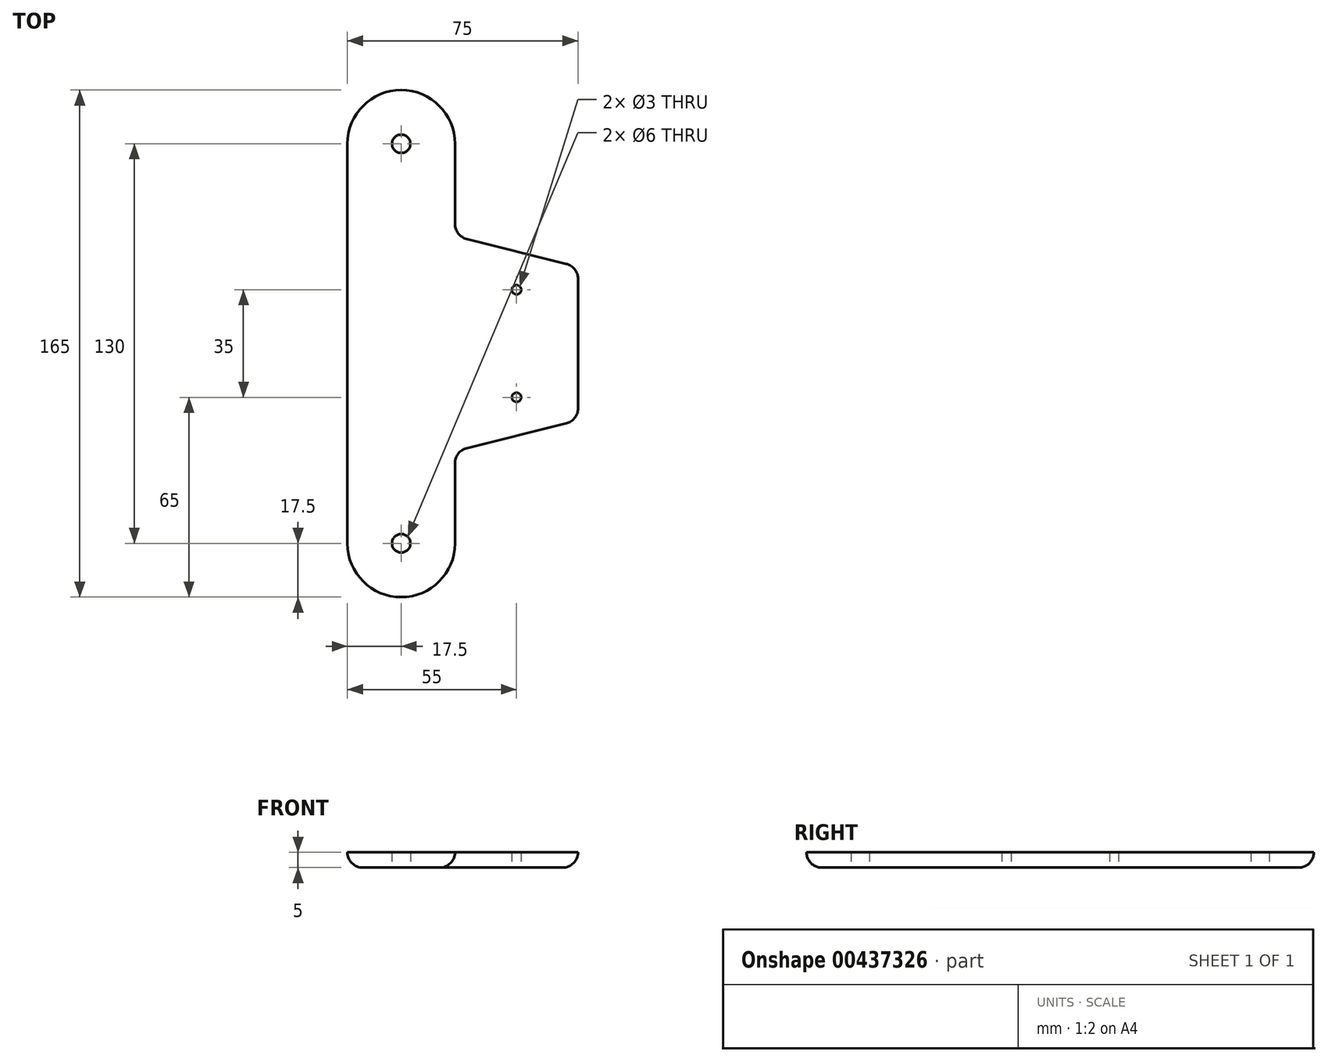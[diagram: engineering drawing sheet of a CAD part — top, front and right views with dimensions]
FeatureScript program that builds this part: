
annotation { "Feature Type Name" : "Feature", "Feature Type Description" : "" }
export const myFeature = defineFeature(function(context is Context, id is Id, definition is map)
    precondition{}
    {
        {
            var Q0;
            Q0=qCreatedBy(makeId("Top.planeOp"),FACE);
            var sketch = newSketch(context, id + "F0", { "sketchPlane" : qUnion([Q0])});
            skLineSegment(sketch, "E0.left", {"start": v(17.5, 65) * mm, "end": v(17.5, -65) * mm});
            skLineSegment(sketch, "E0.right", {"start": v(-17.5, 65) * mm, "end": v(-17.5, 38.9) * mm});
            skPoint(sketch, "E0.middle", {"position": v(0, 0) * mm});
            skArc(sketch, "E1", {"start": v(-17.5, -65) * mm, "mid": v(0, -82.5) * mm, "end": v(17.5, -65) * mm});
            skLineSegment(sketch, "E2.0", {"start": v(-57.5, 21.1) * mm, "end": v(-57.5, -21.1) * mm});
            skArc(sketch, "E3", {"start": v(17.5, 65) * mm, "mid": v(0, 82.5) * mm, "end": v(-17.5, 65) * mm});
            skLineSegment(sketch, "E4", {"start": v(-53.71, -25.95) * mm, "end": v(-21.29, -34.05) * mm});
            skLineSegment(sketch, "E5", {"start": v(-53.71, 25.95) * mm, "end": v(-21.29, 34.05) * mm});
            skLineSegment(sketch, "E6.trimOffspring", {"start": v(-17.5, -38.9) * mm, "end": v(-17.5, -65) * mm});
            skPoint(sketch, "E7.visualSharp", {"position": v(-57.5, 25) * mm});
            skArc(sketch, "E7.filletArc", {"start": v(-53.71, 25.95) * mm, "mid": v(-56.44, 24.17) * mm, "end": v(-57.5, 21.1) * mm});
            skPoint(sketch, "E8.visualSharp", {"position": v(-57.5, -25) * mm});
            skArc(sketch, "E8.filletArc", {"start": v(-57.5, -21.1) * mm, "mid": v(-56.44, -24.17) * mm, "end": v(-53.71, -25.95) * mm});
            skPoint(sketch, "E9.visualSharp", {"position": v(-17.5, -35) * mm});
            skArc(sketch, "E9.filletArc", {"start": v(-17.5, -38.9) * mm, "mid": v(-18.56, -35.83) * mm, "end": v(-21.29, -34.05) * mm});
            skPoint(sketch, "E10.visualSharp", {"position": v(-17.5, 35) * mm});
            skArc(sketch, "E10.filletArc", {"start": v(-21.29, 34.05) * mm, "mid": v(-18.56, 35.83) * mm, "end": v(-17.5, 38.9) * mm});
            skPoint(sketch, "E11", {"position": v(-57.5, 0) * mm});
            skPoint(sketch, "E12", {"position": v(-37.5, 0) * mm});
            skCircle(sketch, "E13", {"center": v(-37.5, 17.5) * mm, "radius": 1.5 * mm});
            skLineSegment(sketch, "E14", {"start": v(-57.5, 0) * mm, "end": v(0, 0) * mm, "construction": true});
            skCircle(sketch, "E15.MirrorC", {"center": v(-37.5, -17.5) * mm, "radius": 1.5 * mm});
            skCircle(sketch, "E16", {"center": v(0, 65) * mm, "radius": 3 * mm});
            skCircle(sketch, "E17", {"center": v(0, -65) * mm, "radius": 3 * mm});
            skSolve(sketch);
        }
        {
            var Q0;
            Q0=makeQuery(id+"F0.imprint","IMPRINT",FACE,{"disambiguationData":[TD([[makeQuery(id+"F0.imprint","IMPRINT",EDGE,{"derivedFrom":sQuery(id+"F0.wireOp",EDGE,"E0.left")}),-1.0]])]});
            extrude(context, id + "F1", {"entities" : qUnion([Q0]), "depth" : 5 * mm});
        }
        {
            var Q0;
            Q0=makeQuery(id+"F1.opExtrude","CAP_EDGE",EDGE,{"disambiguationData":[OSD([sQuery(id+"F0.wireOp",EDGE,"E0.left")])],"isStart":true});
            fillet(context, id + "F2", {"entities" : qUnion([Q0]), "radius" : 5 * mm, "tangentPropagation" : true, "allowEdgeOverflow" : false});
        }
        {
            var Q0;
            Q0=makeQuery(id+"F1.opExtrude","SWEPT_BODY",BODY,{"disambiguationData":[OSD([sQuery(id+"F0.wireOp",EDGE,"E0.left"),sQuery(id+"F0.wireOp",EDGE,"E0.right"),sQuery(id+"F0.wireOp",EDGE,"E1"),sQuery(id+"F0.wireOp",EDGE,"E2.0"),sQuery(id+"F0.wireOp",EDGE,"E3"),sQuery(id+"F0.wireOp",EDGE,"E4"),sQuery(id+"F0.wireOp",EDGE,"E5"),sQuery(id+"F0.wireOp",EDGE,"E6.trimOffspring"),sQuery(id+"F0.wireOp",EDGE,"E7.filletArc"),sQuery(id+"F0.wireOp",EDGE,"E8.filletArc"),sQuery(id+"F0.wireOp",EDGE,"E9.filletArc"),sQuery(id+"F0.wireOp",EDGE,"E10.filletArc"),sQuery(id+"F0.wireOp",EDGE,"E13"),sQuery(id+"F0.wireOp",EDGE,"E15.MirrorC")])]});
            var Q1;
            Q1=qCreatedBy(makeId("Right.planeOp"),FACE);
            mirror(context, id + "F3", {"entities" : qUnion([Q0]), "mirrorPlane" : qUnion([Q1])});
        }
        {
            var Q0;
            Q0=makeQuery(id+"F1.opExtrude","SWEPT_BODY",BODY,{"disambiguationData":[OSD([sQuery(id+"F0.wireOp",EDGE,"E0.left"),sQuery(id+"F0.wireOp",EDGE,"E0.right"),sQuery(id+"F0.wireOp",EDGE,"E1"),sQuery(id+"F0.wireOp",EDGE,"E2.0"),sQuery(id+"F0.wireOp",EDGE,"E3"),sQuery(id+"F0.wireOp",EDGE,"E4"),sQuery(id+"F0.wireOp",EDGE,"E5"),sQuery(id+"F0.wireOp",EDGE,"E6.trimOffspring"),sQuery(id+"F0.wireOp",EDGE,"E7.filletArc"),sQuery(id+"F0.wireOp",EDGE,"E8.filletArc"),sQuery(id+"F0.wireOp",EDGE,"E9.filletArc"),sQuery(id+"F0.wireOp",EDGE,"E10.filletArc"),sQuery(id+"F0.wireOp",EDGE,"E13"),sQuery(id+"F0.wireOp",EDGE,"E15.MirrorC")])]});
            deleteBodies(context, id + "F4", {"entities" : qUnion([Q0])});
        }
    });
